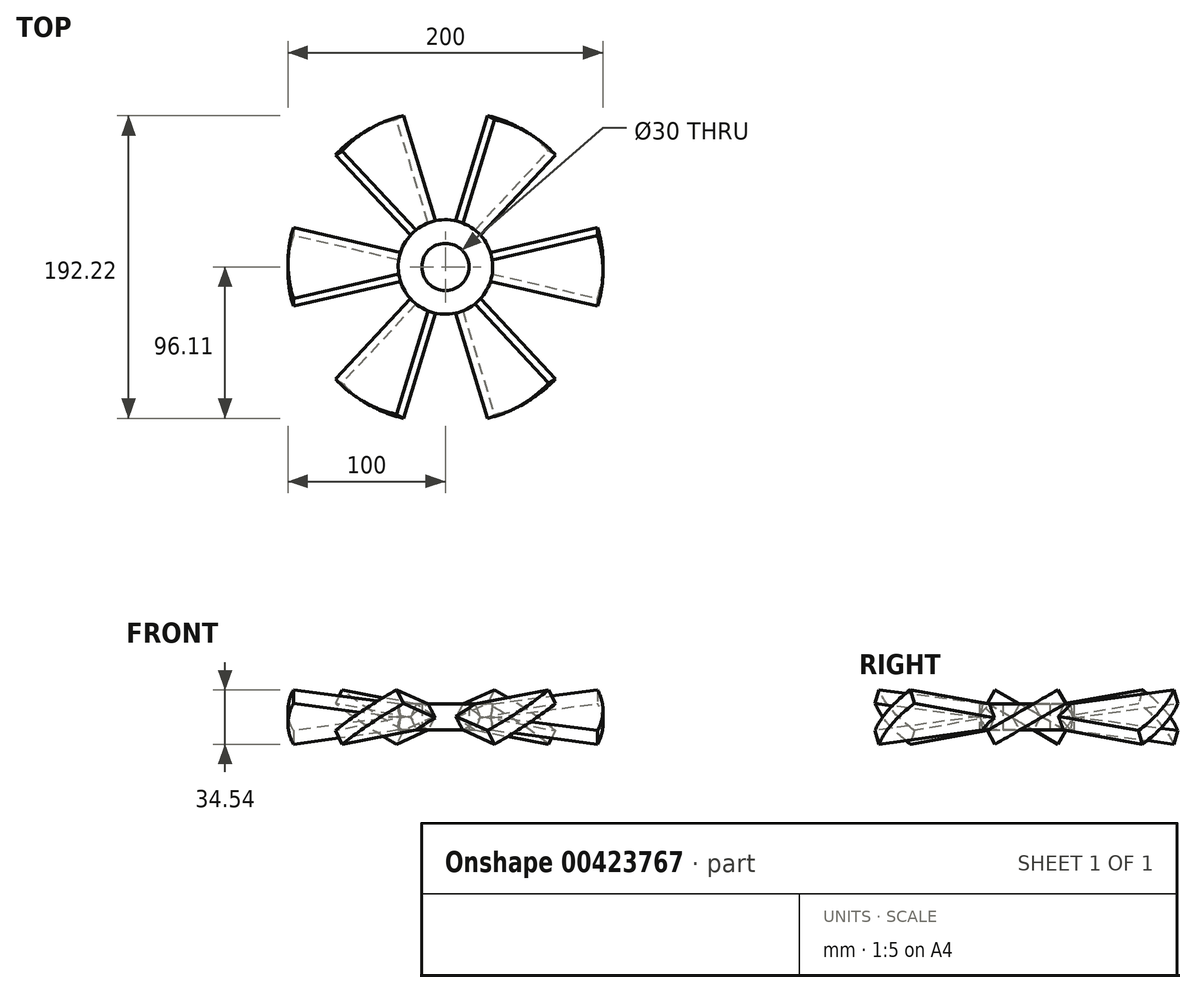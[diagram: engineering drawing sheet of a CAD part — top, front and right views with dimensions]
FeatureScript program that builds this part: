
annotation { "Feature Type Name" : "Feature", "Feature Type Description" : "" }
export const myFeature = defineFeature(function(context is Context, id is Id, definition is map)
    precondition{}
    {
        {
            var Q0;
            Q0=qCreatedBy(makeId("Top.planeOp"),FACE);
            var sketch = newSketch(context, id + "F0", { "sketchPlane" : qUnion([Q0])});
            skCircle(sketch, "E0", {"center": v(0, 0) * mm, "radius": 30 * mm});
            skCircle(sketch, "E1", {"center": v(0, 0) * mm, "radius": 100 * mm});
            skCircle(sketch, "E2", {"center": v(0, 0) * mm, "radius": 15 * mm});
            skLineSegment(sketch, "E3", {"start": v(0, 0) * mm, "end": v(44.96, 0) * mm});
            skPoint(sketch, "E4.endSnap0", {"position": v(22.48, 0) * mm});
            skLineSegment(sketch, "E5.MirrorCS", {"start": v(0, 0) * mm, "end": v(96.6, -25.88) * mm});
            skLineSegment(sketch, "E6", {"start": v(0, 0) * mm, "end": v(96.6, 25.88) * mm});
            skSolve(sketch);
        }
        {
            var Q0;
            {var subQ5=sQuery(id+"F0.wireOp",EDGE,"E0");var subQ8=makeQuery(id+"F0.imprint","INTERSECT",VERTEX,{"derivedFrom":[subQ5,sQuery(id+"F0.wireOp",EDGE,"E3")]});Q0=makeQuery(id+"F0.imprint","IMPRINT",FACE,{"disambiguationData":[TD([[makeQuery(id+"F0.imprint","IMPRINT",EDGE,{"disambiguationData":[TD([[subQ8,-1.0]])],"derivedFrom":subQ5}),-1.0]])]});}
            var Q1;
            {var subQ0=sQuery(id+"F0.wireOp",EDGE,"E3");var subQ1=sQuery(id+"F0.wireOp",EDGE,"E0");var subQ2=makeQuery(id+"F0.imprint","INTERSECT",VERTEX,{"derivedFrom":[subQ1,subQ0]});Q1=makeQuery(id+"F0.imprint","IMPRINT",FACE,{"disambiguationData":[TD([[makeQuery(id+"F0.imprint","IMPRINT",EDGE,{"disambiguationData":[TD([[subQ2,1.0]])],"derivedFrom":subQ1}),1.0]])]});}
            var Q2;
            {var subQ0=sQuery(id+"F0.wireOp",EDGE,"E3");var subQ1=sQuery(id+"F0.wireOp",EDGE,"E0");var subQ2=makeQuery(id+"F0.imprint","INTERSECT",VERTEX,{"derivedFrom":[subQ1,subQ0]});Q2=makeQuery(id+"F0.imprint","IMPRINT",FACE,{"disambiguationData":[TD([[makeQuery(id+"F0.imprint","IMPRINT",EDGE,{"disambiguationData":[TD([[subQ2,-1.0]])],"derivedFrom":subQ1}),1.0]])]});}
            extrude(context, id + "F1", {"entities" : qUnion([Q0, Q1, Q2]), "endBound" : BoundingType.SYMMETRIC, "depth" : 10 * mm});
        }
        {
            var Q0;
            Q0=makeQuery(id+"F1.opExtrude","SWEPT_BODY",BODY,{"disambiguationData":[OSD([sQuery(id+"F0.wireOp",EDGE,"E1"),sQuery(id+"F0.wireOp",EDGE,"E2"),sQuery(id+"F0.wireOp",EDGE,"E5.MirrorCS"),sQuery(id+"F0.wireOp",EDGE,"E6")])]});
            var Q1;
            Q1=sQuery(id+"F0.wireOp",EDGE,"E3");
            var Q2;
            Q2=sQuery(id+"F0.wireOp",EDGE,"E3");
            transform(context, id + "F2", {"entities" : qUnion([Q0]), "transformType" : TransformType.ROTATION, "transformAxis" : qUnion([Q2]), "angle" : 30 * degree, "makeCopy" : false});
        }
        {
            var Q0;
            Q0=qCreatedBy(makeId("Front.planeOp"),FACE);
            var sketch = newSketch(context, id + "F3", { "sketchPlane" : qUnion([Q0])});
            skLineSegment(sketch, "E7", {"start": v(0, -14) * mm, "end": v(0, 46.1) * mm, "construction": true});
            skSolve(sketch);
        }
        {
            var Q0;
            Q0=makeQuery(id+"F1.opExtrude","SWEPT_BODY",BODY,{"disambiguationData":[OSD([sQuery(id+"F0.wireOp",EDGE,"E1"),sQuery(id+"F0.wireOp",EDGE,"E2"),sQuery(id+"F0.wireOp",EDGE,"E5.MirrorCS"),sQuery(id+"F0.wireOp",EDGE,"E6")])]});
            var Q1;
            Q1=sQuery(id+"F3.wireOp",EDGE,"E7");
            circularPattern(context, id + "F4", {"entities" : qUnion([Q0]), "axis" : qUnion([Q1]), "angle" : 360 * degree, "instanceCount" : 6, "equalSpace" : true});
        }
        {
            var Q0;
            {var subQ0=sQuery(id+"F0.wireOp",EDGE,"E6");var subQ1=sQuery(id+"F0.wireOp",EDGE,"E0");var subQ2=makeQuery(id+"F0.imprint","INTERSECT",VERTEX,{"derivedFrom":[subQ1,subQ0]});Q0=makeQuery(id+"F0.imprint","IMPRINT",FACE,{"disambiguationData":[TD([[makeQuery(id+"F0.imprint","IMPRINT",EDGE,{"disambiguationData":[TD([[subQ2,-1.0]])],"derivedFrom":subQ1}),1.0]])]});}
            var Q1;
            {var subQ0=sQuery(id+"F0.wireOp",EDGE,"E3");var subQ1=sQuery(id+"F0.wireOp",EDGE,"E0");var subQ2=makeQuery(id+"F0.imprint","INTERSECT",VERTEX,{"derivedFrom":[subQ1,subQ0]});Q1=makeQuery(id+"F0.imprint","IMPRINT",FACE,{"disambiguationData":[TD([[makeQuery(id+"F0.imprint","IMPRINT",EDGE,{"disambiguationData":[TD([[subQ2,1.0]])],"derivedFrom":subQ1}),1.0]])]});}
            var Q2;
            {var subQ0=sQuery(id+"F0.wireOp",EDGE,"E3");var subQ1=sQuery(id+"F0.wireOp",EDGE,"E0");var subQ2=makeQuery(id+"F0.imprint","INTERSECT",VERTEX,{"derivedFrom":[subQ1,subQ0]});Q2=makeQuery(id+"F0.imprint","IMPRINT",FACE,{"disambiguationData":[TD([[makeQuery(id+"F0.imprint","IMPRINT",EDGE,{"disambiguationData":[TD([[subQ2,-1.0]])],"derivedFrom":subQ1}),1.0]])]});}
            var Q3;
            {var subQ0=sQuery(id+"F0.wireOp",EDGE,"E3");var subQ1=sQuery(id+"F0.wireOp",EDGE,"E2");var subQ2=makeQuery(id+"F0.imprint","INTERSECT",VERTEX,{"derivedFrom":[subQ1,subQ0]});Q3=makeQuery(id+"F0.imprint","IMPRINT",FACE,{"disambiguationData":[TD([[makeQuery(id+"F0.imprint","IMPRINT",EDGE,{"disambiguationData":[TD([[subQ2,1.0]])],"derivedFrom":subQ1}),1.0]])]});}
            var Q4;
            {var subQ0=sQuery(id+"F0.wireOp",EDGE,"E6");var subQ1=sQuery(id+"F0.wireOp",EDGE,"E2");var subQ2=makeQuery(id+"F0.imprint","INTERSECT",VERTEX,{"derivedFrom":[subQ1,subQ0]});Q4=makeQuery(id+"F0.imprint","IMPRINT",FACE,{"disambiguationData":[TD([[makeQuery(id+"F0.imprint","IMPRINT",EDGE,{"disambiguationData":[TD([[subQ2,-1.0]])],"derivedFrom":subQ1}),1.0]])]});}
            var Q5;
            {var subQ0=sQuery(id+"F0.wireOp",EDGE,"E6");var subQ1=sQuery(id+"F0.wireOp",EDGE,"E2");var subQ2=makeQuery(id+"F0.imprint","INTERSECT",VERTEX,{"derivedFrom":[subQ1,subQ0]});Q5=makeQuery(id+"F0.imprint","IMPRINT",FACE,{"disambiguationData":[TD([[makeQuery(id+"F0.imprint","IMPRINT",EDGE,{"disambiguationData":[TD([[subQ2,1.0]])],"derivedFrom":subQ1}),1.0]])]});}
            extrude(context, id + "F5", {"entities" : qUnion([Q0, Q1, Q2, Q3, Q4, Q5]), "operationType" : NewBodyOperationType.REMOVE, "endBound" : BoundingType.SYMMETRIC, "depth" : 25 * mm});
        }
        {
            var Q0;
            {var subQ0=sQuery(id+"F0.wireOp",EDGE,"E6");var subQ1=sQuery(id+"F0.wireOp",EDGE,"E0");var subQ2=makeQuery(id+"F0.imprint","INTERSECT",VERTEX,{"derivedFrom":[subQ1,subQ0]});Q0=makeQuery(id+"F0.imprint","IMPRINT",FACE,{"disambiguationData":[TD([[makeQuery(id+"F0.imprint","IMPRINT",EDGE,{"disambiguationData":[TD([[subQ2,-1.0]])],"derivedFrom":subQ1}),1.0]])]});}
            var Q1;
            {var subQ0=sQuery(id+"F0.wireOp",EDGE,"E3");var subQ1=sQuery(id+"F0.wireOp",EDGE,"E0");var subQ2=makeQuery(id+"F0.imprint","INTERSECT",VERTEX,{"derivedFrom":[subQ1,subQ0]});Q1=makeQuery(id+"F0.imprint","IMPRINT",FACE,{"disambiguationData":[TD([[makeQuery(id+"F0.imprint","IMPRINT",EDGE,{"disambiguationData":[TD([[subQ2,1.0]])],"derivedFrom":subQ1}),1.0]])]});}
            var Q2;
            {var subQ0=sQuery(id+"F0.wireOp",EDGE,"E3");var subQ1=sQuery(id+"F0.wireOp",EDGE,"E0");var subQ2=makeQuery(id+"F0.imprint","INTERSECT",VERTEX,{"derivedFrom":[subQ1,subQ0]});Q2=makeQuery(id+"F0.imprint","IMPRINT",FACE,{"disambiguationData":[TD([[makeQuery(id+"F0.imprint","IMPRINT",EDGE,{"disambiguationData":[TD([[subQ2,-1.0]])],"derivedFrom":subQ1}),1.0]])]});}
            var Q3;
            {var subQ0=sQuery(id+"F0.wireOp",EDGE,"E6");Q3=makeQuery(id+"F5.boolean.opBoolean","INTERSECT",VERTEX,{"derivedFrom":[makeQuery(id+"F1.opExtrude","CAP_FACE",FACE,{"disambiguationData":[OSD([sQuery(id+"F0.wireOp",EDGE,"E1"),sQuery(id+"F0.wireOp",EDGE,"E2"),sQuery(id+"F0.wireOp",EDGE,"E5.MirrorCS"),subQ0])],"isStart":false}),makeQuery(id+"F1.opExtrude","SWEPT_FACE",FACE,{"disambiguationData":[OSD([subQ0])]}),makeQuery(id+"F5.opExtrude","SWEPT_FACE",FACE,{"disambiguationData":[OSD([sQuery(id+"F0.wireOp",EDGE,"E0")])]})]});}
            var Q4;
            {var subQ0=sQuery(id+"F0.wireOp",EDGE,"E5.MirrorCS");Q4=makeQuery(id+"F5.boolean.opBoolean","INTERSECT",VERTEX,{"derivedFrom":[makeQuery(id+"F4.opPattern","COPY",FACE,{"derivedFrom":makeQuery(id+"F1.opExtrude","CAP_FACE",FACE,{"disambiguationData":[OSD([sQuery(id+"F0.wireOp",EDGE,"E1"),sQuery(id+"F0.wireOp",EDGE,"E2"),subQ0,sQuery(id+"F0.wireOp",EDGE,"E6")])],"isStart":true}),"instanceName":"4"}),makeQuery(id+"F4.opPattern","COPY",FACE,{"derivedFrom":makeQuery(id+"F1.opExtrude","SWEPT_FACE",FACE,{"disambiguationData":[OSD([subQ0])]}),"instanceName":"4"}),makeQuery(id+"F5.opExtrude","SWEPT_FACE",FACE,{"disambiguationData":[OSD([sQuery(id+"F0.wireOp",EDGE,"E0")])]})]});}
            extrude(context, id + "F6", {"entities" : qUnion([Q0, Q1, Q2]), "operationType" : NewBodyOperationType.ADD, "endBound" : BoundingType.UP_TO_VERTEX, "endBoundEntityVertex" : qUnion([Q3]), "depth" : 25 * mm, "hasSecondDirection" : true, "secondDirectionBound" : SecondDirectionBoundingType.UP_TO_VERTEX, "secondDirectionOppositeDirection" : true, "secondDirectionBoundEntityVertex" : qUnion([Q4]), "secondDirectionDepth" : 25 * mm});
        }
    });
